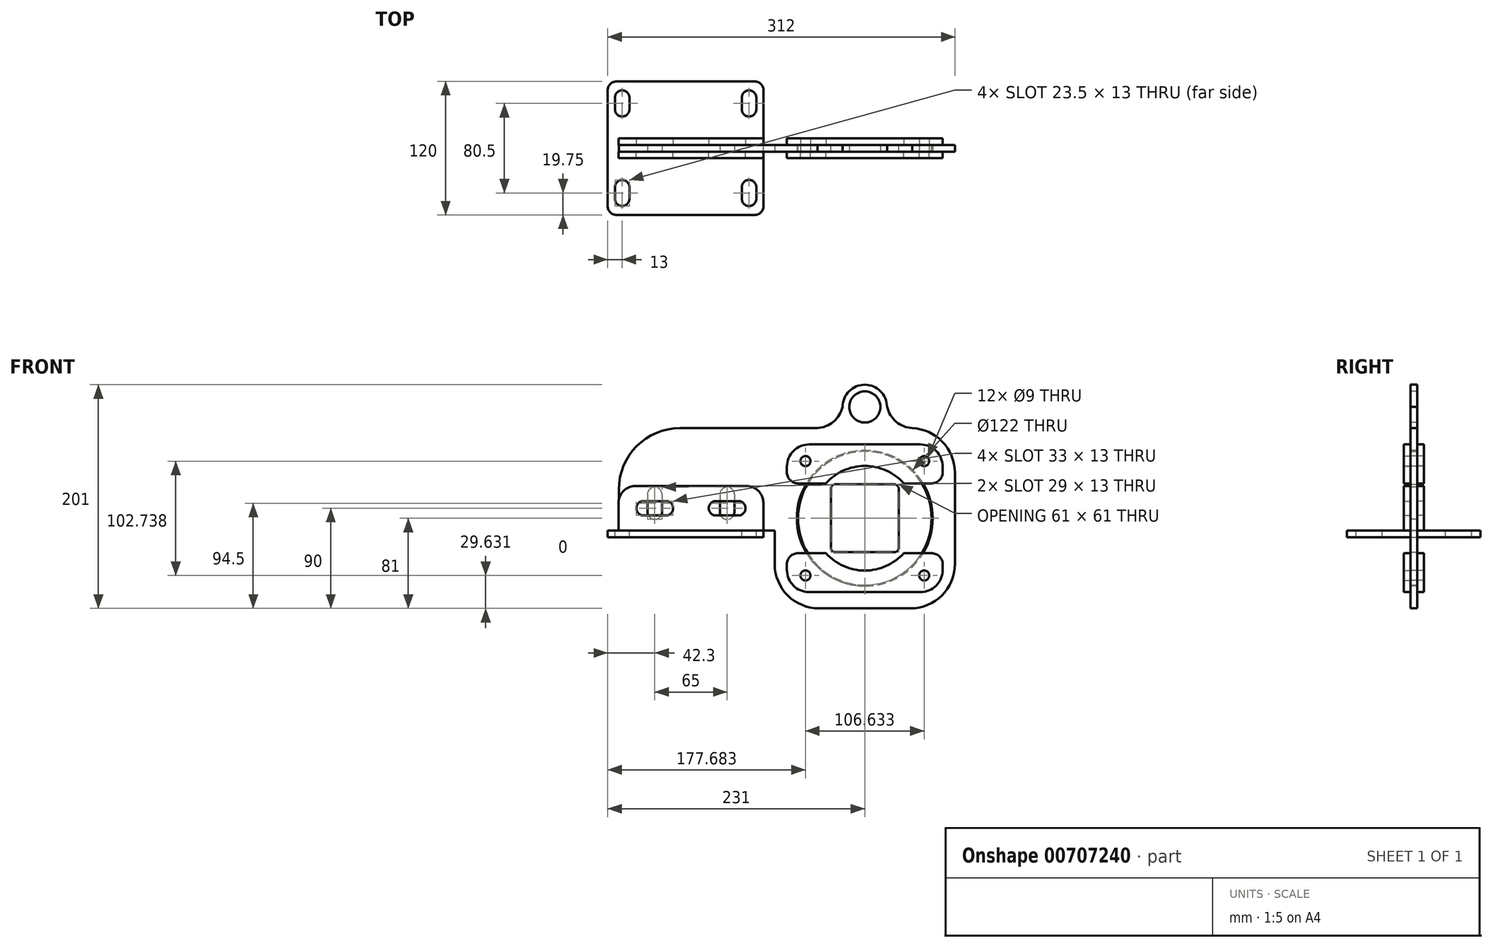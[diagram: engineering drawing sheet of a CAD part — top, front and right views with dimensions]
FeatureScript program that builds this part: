
annotation { "Feature Type Name" : "Feature", "Feature Type Description" : "" }
export const myFeature = defineFeature(function(context is Context, id is Id, definition is map)
    precondition{}
    {
        {
            var Q0;
            Q0=qCreatedBy(makeId("Front.planeOp"),FACE);
            var sketch = newSketch(context, id + "F0", { "sketchPlane" : qUnion([Q0])});
            skPoint(sketch, "E0", {"position": v(0, 0) * mm});
            skLineSegment(sketch, "E1.bottom", {"start": v(26.5, 30.5) * mm, "end": v(-26.5, 30.5) * mm});
            skLineSegment(sketch, "E1.top", {"start": v(26.5, -30.5) * mm, "end": v(-26.5, -30.5) * mm});
            skLineSegment(sketch, "E1.left", {"start": v(30.5, 26.5) * mm, "end": v(30.5, -26.5) * mm});
            skLineSegment(sketch, "E1.right", {"start": v(-30.5, 26.5) * mm, "end": v(-30.5, -26.5) * mm});
            skCircle(sketch, "E2", {"center": v(0, 0) * mm, "radius": 60 * mm});
            skPoint(sketch, "E3.visualSharp", {"position": v(-30.5, 30.5) * mm});
            skArc(sketch, "E3.filletArc", {"start": v(-26.5, 30.5) * mm, "mid": v(-29.33, 29.33) * mm, "end": v(-30.5, 26.5) * mm});
            skPoint(sketch, "E4.visualSharp", {"position": v(30.5, 30.5) * mm});
            skArc(sketch, "E4.filletArc", {"start": v(30.5, 26.5) * mm, "mid": v(29.33, 29.33) * mm, "end": v(26.5, 30.5) * mm});
            skPoint(sketch, "E5.visualSharp", {"position": v(30.5, -30.5) * mm});
            skArc(sketch, "E5.filletArc", {"start": v(26.5, -30.5) * mm, "mid": v(29.33, -29.33) * mm, "end": v(30.5, -26.5) * mm});
            skPoint(sketch, "E6.visualSharp", {"position": v(-30.5, -30.5) * mm});
            skArc(sketch, "E6.filletArc", {"start": v(-30.5, -26.5) * mm, "mid": v(-29.33, -29.33) * mm, "end": v(-26.5, -30.5) * mm});
            skSolve(sketch);
        }
        {
            var Q0;
            Q0 = qSketchRegion(id + "F0", true);
            extrude(context, id + "F1", {"entities" : qUnion([Q0]), "depth" : 6 * mm, "offsetDistance" : 25 * mm});
        }
        {
            var Q0;
            Q0=makeQuery(id+"F1.opExtrude","CAP_FACE",FACE,{"disambiguationData":[OSD([sQuery(id+"F0.wireOp",EDGE,"E1.bottom"),sQuery(id+"F0.wireOp",EDGE,"E1.top"),sQuery(id+"F0.wireOp",EDGE,"E1.left"),sQuery(id+"F0.wireOp",EDGE,"E1.right"),sQuery(id+"F0.wireOp",EDGE,"E2"),sQuery(id+"F0.wireOp",EDGE,"E3.filletArc"),sQuery(id+"F0.wireOp",EDGE,"E4.filletArc"),sQuery(id+"F0.wireOp",EDGE,"E5.filletArc"),sQuery(id+"F0.wireOp",EDGE,"E6.filletArc")])],"isStart":false});
            var sketch = newSketch(context, id + "F2", { "sketchPlane" : qUnion([Q0])});
            skCircle(sketch, "E7.0", {"center": v(0, 0) * mm, "radius": 61 * mm});
            skLineSegment(sketch, "E8.top", {"start": v(41, -81) * mm, "end": v(-41, -81) * mm});
            skLineSegment(sketch, "E8.left", {"start": v(81, 41) * mm, "end": v(81, -41) * mm});
            skLineSegment(sketch, "E8.right", {"start": v(-81, -19) * mm, "end": v(-81, -41) * mm});
            skLineSegment(sketch, "E9.bottom", {"start": v(-81, 81) * mm, "end": v(-166, 81) * mm});
            skPoint(sketch, "E10.visualSharp", {"position": v(-81, -81) * mm});
            skArc(sketch, "E10.filletArc", {"start": v(-81, -41) * mm, "mid": v(-69.28, -69.28) * mm, "end": v(-41, -81) * mm});
            skPoint(sketch, "E11.visualSharp", {"position": v(81, -81) * mm});
            skArc(sketch, "E11.filletArc", {"start": v(41, -81) * mm, "mid": v(69.28, -69.28) * mm, "end": v(81, -41) * mm});
            skPoint(sketch, "E12.visualSharp", {"position": v(81, 81) * mm});
            skArc(sketch, "E12.filletArc", {"start": v(81, 41) * mm, "mid": v(69.75, 68.81) * mm, "end": v(42.32, 80.98) * mm});
            skLineSegment(sketch, "E13", {"start": v(0, 0) * mm, "end": v(0, 100) * mm, "construction": true});
            skPoint(sketch, "E13.endSnap0", {"position": v(0, 30.5) * mm});
            skPoint(sketch, "E14.endSnap0", {"position": v(-20, 81) * mm});
            skArc(sketch, "E15.MirrorCS", {"start": v(42.5, 81) * mm, "mid": v(42.41, 80.99) * mm, "end": v(42.32, 80.98) * mm});
            skArc(sketch, "E16.trimOffspring", {"start": v(20, 100) * mm, "mid": v(0, 120) * mm, "end": v(-20, 100) * mm});
            skLineSegment(sketch, "E17.trimOffspring", {"start": v(-42.5, 81) * mm, "end": v(-81, 81) * mm});
            skCircle(sketch, "E18", {"center": v(0, 100) * mm, "radius": 14 * mm});
            skLineSegment(sketch, "E19", {"start": v(-90.5, -11) * mm, "end": v(-90.5, 81) * mm, "construction": true});
            skLineSegment(sketch, "E20", {"start": v(-211, 81) * mm, "end": v(-221, 81) * mm});
            skLineSegment(sketch, "E21", {"start": v(-221, 26) * mm, "end": v(-221, -11) * mm});
            skLineSegment(sketch, "E22", {"start": v(-221, -11) * mm, "end": v(-81, -11) * mm});
            skLineSegment(sketch, "E23", {"start": v(-81, -11) * mm, "end": v(-81, -19) * mm});
            skPoint(sketch, "E24.end.orphan", {"position": v(-211, -19) * mm});
            skPoint(sketch, "E25.orphan", {"position": v(-221, -19) * mm});
            skPoint(sketch, "E26.newPointA", {"position": v(-221, 81) * mm});
            skPoint(sketch, "E26.newPointB", {"position": v(-211, 81) * mm});
            skArc(sketch, "E26.filletArc", {"start": v(-166, 81) * mm, "mid": v(-204.9, 64.9) * mm, "end": v(-221, 26) * mm});
            skPoint(sketch, "E8.bottom.end.orphan", {"position": v(42.5, 81) * mm});
            skPoint(sketch, "E8.bottom.start.orphan", {"position": v(41, 81) * mm});
            skArc(sketch, "E27", {"start": v(-42.5, 81) * mm, "mid": v(-28.16, 86.84) * mm, "end": v(-20, 100) * mm});
            skArc(sketch, "E28.MirrorCS", {"start": v(42.5, 81) * mm, "mid": v(28.16, 86.84) * mm, "end": v(20, 100) * mm});
            skSolve(sketch);
        }
        {
            var Q0;
            Q0 = qSketchRegion(id + "F2", true);
            extrude(context, id + "F3", {"entities" : qUnion([Q0]), "oppositeDirection" : true, "depth" : 6 * mm, "offsetDistance" : 25 * mm});
        }
        {
            var Q0;
            Q0=makeQuery(id+"F3.opExtrude","CAP_FACE",FACE,{"disambiguationData":[OSD([sQuery(id+"F2.wireOp",EDGE,"E7.0"),sQuery(id+"F2.wireOp",EDGE,"E8.bottom"),sQuery(id+"F2.wireOp",EDGE,"E8.top"),sQuery(id+"F2.wireOp",EDGE,"E8.left"),sQuery(id+"F2.wireOp",EDGE,"E8.right"),sQuery(id+"F2.wireOp",EDGE,"E9.bottom"),sQuery(id+"F2.wireOp",EDGE,"E9.top"),sQuery(id+"F2.wireOp",EDGE,"E9.right"),sQuery(id+"F2.wireOp",EDGE,"338df59d-56eb-4721-a302-496fc696f20b.0.startCap"),sQuery(id+"F2.wireOp",EDGE,"338df59d-56eb-4721-a302-496fc696f20b.0.endCap"),sQuery(id+"F2.wireOp",EDGE,"338df59d-56eb-4721-a302-496fc696f20b.0.left"),sQuery(id+"F2.wireOp",EDGE,"338df59d-56eb-4721-a302-496fc696f20b.0.right"),sQuery(id+"F2.wireOp",EDGE,"338df59d-56eb-4721-a302-496fc696f20b.1.startCap"),sQuery(id+"F2.wireOp",EDGE,"338df59d-56eb-4721-a302-496fc696f20b.1.endCap"),sQuery(id+"F2.wireOp",EDGE,"338df59d-56eb-4721-a302-496fc696f20b.1.left"),sQuery(id+"F2.wireOp",EDGE,"338df59d-56eb-4721-a302-496fc696f20b.1.right"),sQuery(id+"F2.wireOp",EDGE,"E10.filletArc"),sQuery(id+"F2.wireOp",EDGE,"E11.filletArc"),sQuery(id+"F2.wireOp",EDGE,"E12.filletArc")])],"isStart":true});
            var sketch = newSketch(context, id + "F4", { "sketchPlane" : qUnion([Q0])});
            skArc(sketch, "E29.0", {"start": v(-35, -31.37) * mm, "mid": v(0, -47) * mm, "end": v(35, -31.37) * mm});
            skLineSegment(sketch, "E30", {"start": v(-60, 31.37) * mm, "end": v(-35, 31.37) * mm});
            skLineSegment(sketch, "E31", {"start": v(0, 0) * mm, "end": v(0, 41.73) * mm, "construction": true});
            skLineSegment(sketch, "E32", {"start": v(-70, 41.37) * mm, "end": v(-70, 46.37) * mm});
            skLineSegment(sketch, "E33", {"start": v(70, 41.37) * mm, "end": v(70, 46.37) * mm});
            skLineSegment(sketch, "E34", {"start": v(50, 66.37) * mm, "end": v(-50, 66.37) * mm});
            skPoint(sketch, "E35.visualSharp", {"position": v(70, 66.37) * mm});
            skArc(sketch, "E35.filletArc", {"start": v(70, 46.37) * mm, "mid": v(64.14, 60.51) * mm, "end": v(50, 66.37) * mm});
            skPoint(sketch, "E36.visualSharp", {"position": v(-70, 66.37) * mm});
            skArc(sketch, "E36.filletArc", {"start": v(-50, 66.37) * mm, "mid": v(-64.14, 60.51) * mm, "end": v(-70, 46.37) * mm});
            skPoint(sketch, "E37.visualSharp", {"position": v(-70, 31.37) * mm});
            skArc(sketch, "E37.filletArc", {"start": v(-70, 41.37) * mm, "mid": v(-67.07, 34.3) * mm, "end": v(-60, 31.37) * mm});
            skPoint(sketch, "E38.visualSharp", {"position": v(70, 31.37) * mm});
            skArc(sketch, "E38.filletArc", {"start": v(60, 31.37) * mm, "mid": v(67.07, 34.3) * mm, "end": v(70, 41.37) * mm});
            skLineSegment(sketch, "E39.trimOffspring", {"start": v(35, 31.37) * mm, "end": v(60, 31.37) * mm});
            skCircle(sketch, "E40", {"center": v(-53.32, 51.37) * mm, "radius": 4.5 * mm});
            skCircle(sketch, "E41.MirrorC", {"center": v(53.32, 51.37) * mm, "radius": 4.5 * mm});
            skLineSegment(sketch, "E42", {"start": v(0, 0) * mm, "end": v(-70.6, 0) * mm, "construction": true});
            skLineSegment(sketch, "E43", {"start": v(0, 0) * mm, "end": v(70.35, 0) * mm, "construction": true});
            skLineSegment(sketch, "E44.MirrorCS", {"start": v(70, -41.37) * mm, "end": v(70, -46.37) * mm});
            skLineSegment(sketch, "E45.MirrorCS", {"start": v(-70, -41.37) * mm, "end": v(-70, -46.37) * mm});
            skCircle(sketch, "E46.MirrorC", {"center": v(-53.32, -51.37) * mm, "radius": 4.5 * mm});
            skLineSegment(sketch, "E47.MirrorCS", {"start": v(35, -31.37) * mm, "end": v(60, -31.37) * mm});
            skArc(sketch, "E48.MirrorCS", {"start": v(60, -31.37) * mm, "mid": v(67.07, -34.3) * mm, "end": v(70, -41.37) * mm});
            skArc(sketch, "E49.MirrorCS", {"start": v(-70, -41.37) * mm, "mid": v(-67.07, -34.3) * mm, "end": v(-60, -31.37) * mm});
            skPoint(sketch, "E50.MirrorP", {"position": v(70, -31.37) * mm});
            skArc(sketch, "E51.MirrorCS", {"start": v(70, -46.37) * mm, "mid": v(64.14, -60.51) * mm, "end": v(50, -66.37) * mm});
            skPoint(sketch, "E52.MirrorP", {"position": v(-70, -66.37) * mm});
            skPoint(sketch, "E53.MirrorP", {"position": v(-70, -31.37) * mm});
            skLineSegment(sketch, "E54.MirrorCS", {"start": v(-60, -31.37) * mm, "end": v(-35, -31.37) * mm});
            skCircle(sketch, "E55.MirrorC", {"center": v(53.32, -51.37) * mm, "radius": 4.5 * mm});
            skArc(sketch, "E56.MirrorCS", {"start": v(-50, -66.37) * mm, "mid": v(-64.14, -60.51) * mm, "end": v(-70, -46.37) * mm});
            skPoint(sketch, "E57.MirrorP", {"position": v(70, -66.37) * mm});
            skLineSegment(sketch, "E58.MirrorCS", {"start": v(50, -66.37) * mm, "end": v(-50, -66.37) * mm});
            skArc(sketch, "E59.trimOffspring", {"start": v(35, 31.37) * mm, "mid": v(0, 47) * mm, "end": v(-35, 31.37) * mm});
            skSolve(sketch);
        }
        {
            var Q0;
            Q0 = qSketchRegion(id + "F4", true);
            extrude(context, id + "F5", {"entities" : qUnion([Q0]), "depth" : 6 * mm, "offsetDistance" : 25 * mm});
        }
        {
            var Q0;
            Q0=makeQuery(id+"F2.imprint","IMPRINT",FACE,{"disambiguationData":[TD([[makeQuery(id+"F2.imprint","IMPRINT",EDGE,{"derivedFrom":sQuery(id+"F2.wireOp",EDGE,"E7.0")}),-1.0]])]});
            var sketch = newSketch(context, id + "F6", { "sketchPlane" : qUnion([Q0])});
            skCircle(sketch, "E60.0", {"center": v(-53.32, 51.37) * mm, "radius": 4.5 * mm});
            skCircle(sketch, "E61.0", {"center": v(53.32, 51.37) * mm, "radius": 4.5 * mm});
            skCircle(sketch, "E62.0", {"center": v(-53.32, -51.37) * mm, "radius": 4.5 * mm});
            skCircle(sketch, "E63.0", {"center": v(53.32, -51.37) * mm, "radius": 4.5 * mm});
            skSolve(sketch);
        }
        {
            var Q0;
            Q0 = qSketchRegion(id + "F6", true);
            extrude(context, id + "F7", {"entities" : qUnion([Q0]), "operationType" : NewBodyOperationType.REMOVE, "oppositeDirection" : true, "depth" : 25 * mm, "offsetDistance" : 25 * mm});
        }
        {
            var Q0;
            Q0=makeQuery(id+"F3.opExtrude","CAP_FACE",FACE,{"disambiguationData":[OSD([sQuery(id+"F2.wireOp",EDGE,"E7.0"),sQuery(id+"F2.wireOp",EDGE,"E8.bottom"),sQuery(id+"F2.wireOp",EDGE,"E8.top"),sQuery(id+"F2.wireOp",EDGE,"E8.left"),sQuery(id+"F2.wireOp",EDGE,"E8.right"),sQuery(id+"F2.wireOp",EDGE,"E9.bottom"),sQuery(id+"F2.wireOp",EDGE,"E9.top"),sQuery(id+"F2.wireOp",EDGE,"E9.right"),sQuery(id+"F2.wireOp",EDGE,"338df59d-56eb-4721-a302-496fc696f20b.0.startCap"),sQuery(id+"F2.wireOp",EDGE,"338df59d-56eb-4721-a302-496fc696f20b.0.endCap"),sQuery(id+"F2.wireOp",EDGE,"338df59d-56eb-4721-a302-496fc696f20b.0.left"),sQuery(id+"F2.wireOp",EDGE,"338df59d-56eb-4721-a302-496fc696f20b.0.right"),sQuery(id+"F2.wireOp",EDGE,"338df59d-56eb-4721-a302-496fc696f20b.1.startCap"),sQuery(id+"F2.wireOp",EDGE,"338df59d-56eb-4721-a302-496fc696f20b.1.endCap"),sQuery(id+"F2.wireOp",EDGE,"338df59d-56eb-4721-a302-496fc696f20b.1.left"),sQuery(id+"F2.wireOp",EDGE,"338df59d-56eb-4721-a302-496fc696f20b.1.right"),sQuery(id+"F2.wireOp",EDGE,"E10.filletArc"),sQuery(id+"F2.wireOp",EDGE,"E11.filletArc"),sQuery(id+"F2.wireOp",EDGE,"E12.filletArc")])],"isStart":false});
            var sketch = newSketch(context, id + "F8", { "sketchPlane" : qUnion([Q0])});
            skLineSegment(sketch, "E64.0", {"start": v(-35, 31.37) * mm, "end": v(-60, 31.37) * mm});
            skArc(sketch, "E65.0", {"start": v(-35, 31.37) * mm, "mid": v(0, 47) * mm, "end": v(35, 31.37) * mm});
            skLineSegment(sketch, "E66.0", {"start": v(60, 31.37) * mm, "end": v(35, 31.37) * mm});
            skArc(sketch, "E67.0", {"start": v(70, 41.37) * mm, "mid": v(67.07, 34.3) * mm, "end": v(60, 31.37) * mm});
            skArc(sketch, "E68.0", {"start": v(50, 66.37) * mm, "mid": v(64.14, 60.51) * mm, "end": v(70, 46.37) * mm});
            skLineSegment(sketch, "E69.0", {"start": v(70, 41.37) * mm, "end": v(70, 46.37) * mm});
            skCircle(sketch, "E70.0", {"center": v(53.32, 51.37) * mm, "radius": 4.5 * mm});
            skLineSegment(sketch, "E71.0", {"start": v(-50, 66.37) * mm, "end": v(50, 66.37) * mm});
            skArc(sketch, "E72.0", {"start": v(-70, 46.37) * mm, "mid": v(-64.14, 60.51) * mm, "end": v(-50, 66.37) * mm});
            skLineSegment(sketch, "E73.0", {"start": v(-70, 41.37) * mm, "end": v(-70, 46.37) * mm});
            skArc(sketch, "E74.0", {"start": v(-60, 31.37) * mm, "mid": v(-67.07, 34.3) * mm, "end": v(-70, 41.37) * mm});
            skCircle(sketch, "E75.0", {"center": v(-53.32, 51.37) * mm, "radius": 4.5 * mm});
            skLineSegment(sketch, "E76.0", {"start": v(-35, -31.37) * mm, "end": v(-60, -31.37) * mm});
            skArc(sketch, "E77.0", {"start": v(35, -31.37) * mm, "mid": v(0, -47) * mm, "end": v(-35, -31.37) * mm});
            skLineSegment(sketch, "E78.0", {"start": v(60, -31.37) * mm, "end": v(35, -31.37) * mm});
            skArc(sketch, "E79.0", {"start": v(70, -41.37) * mm, "mid": v(67.07, -34.3) * mm, "end": v(60, -31.37) * mm});
            skLineSegment(sketch, "E80.0", {"start": v(70, -41.37) * mm, "end": v(70, -46.37) * mm});
            skArc(sketch, "E81.0", {"start": v(50, -66.37) * mm, "mid": v(64.14, -60.51) * mm, "end": v(70, -46.37) * mm});
            skCircle(sketch, "E82.0", {"center": v(53.32, -51.37) * mm, "radius": 4.5 * mm});
            skLineSegment(sketch, "E83.0", {"start": v(-50, -66.37) * mm, "end": v(50, -66.37) * mm});
            skArc(sketch, "E84.0", {"start": v(-70, -46.37) * mm, "mid": v(-64.14, -60.51) * mm, "end": v(-50, -66.37) * mm});
            skCircle(sketch, "E85.0.0", {"center": v(-53.32, -51.37) * mm, "radius": 4.5 * mm});
            skLineSegment(sketch, "E86.0", {"start": v(-70, -41.37) * mm, "end": v(-70, -46.37) * mm});
            skArc(sketch, "E87.0", {"start": v(-60, -31.37) * mm, "mid": v(-67.07, -34.3) * mm, "end": v(-70, -41.37) * mm});
            skSolve(sketch);
        }
        {
            var Q0;
            Q0 = qSketchRegion(id + "F8", true);
            extrude(context, id + "F9", {"entities" : qUnion([Q0]), "depth" : 6 * mm, "offsetDistance" : 25 * mm});
        }
        {
            var Q0;
            Q0=makeQuery(id+"F3.opExtrude","CAP_FACE",FACE,{"disambiguationData":[OSD([sQuery(id+"F2.wireOp",EDGE,"E7.0"),sQuery(id+"F2.wireOp",EDGE,"E8.bottom"),sQuery(id+"F2.wireOp",EDGE,"E8.top"),sQuery(id+"F2.wireOp",EDGE,"E8.left"),sQuery(id+"F2.wireOp",EDGE,"E8.right"),sQuery(id+"F2.wireOp",EDGE,"E9.bottom"),sQuery(id+"F2.wireOp",EDGE,"E9.top"),sQuery(id+"F2.wireOp",EDGE,"E9.right"),sQuery(id+"F2.wireOp",EDGE,"338df59d-56eb-4721-a302-496fc696f20b.0.startCap"),sQuery(id+"F2.wireOp",EDGE,"338df59d-56eb-4721-a302-496fc696f20b.0.endCap"),sQuery(id+"F2.wireOp",EDGE,"338df59d-56eb-4721-a302-496fc696f20b.0.left"),sQuery(id+"F2.wireOp",EDGE,"338df59d-56eb-4721-a302-496fc696f20b.0.right"),sQuery(id+"F2.wireOp",EDGE,"338df59d-56eb-4721-a302-496fc696f20b.1.startCap"),sQuery(id+"F2.wireOp",EDGE,"338df59d-56eb-4721-a302-496fc696f20b.1.endCap"),sQuery(id+"F2.wireOp",EDGE,"338df59d-56eb-4721-a302-496fc696f20b.1.left"),sQuery(id+"F2.wireOp",EDGE,"338df59d-56eb-4721-a302-496fc696f20b.1.right"),sQuery(id+"F2.wireOp",EDGE,"E10.filletArc"),sQuery(id+"F2.wireOp",EDGE,"E11.filletArc"),sQuery(id+"F2.wireOp",EDGE,"E12.filletArc")])],"isStart":true});
            var sketch = newSketch(context, id + "F10", { "sketchPlane" : qUnion([Q0])});
            skLineSegment(sketch, "E88.0", {"start": v(-91.2, -11) * mm, "end": v(-221.2, -11) * mm});
            skArc(sketch, "E89.0", {"start": v(-178.7, 15.5) * mm, "mid": v(-172.2, 9) * mm, "end": v(-178.7, 2.5) * mm});
            skLineSegment(sketch, "E90.0", {"start": v(-198.7, 2.5) * mm, "end": v(-178.7, 2.5) * mm});
            skArc(sketch, "E91.0", {"start": v(-198.7, 2.5) * mm, "mid": v(-205.2, 9) * mm, "end": v(-198.7, 15.5) * mm});
            skLineSegment(sketch, "E92.0", {"start": v(-198.7, 15.5) * mm, "end": v(-178.7, 15.5) * mm});
            skLineSegment(sketch, "E93.0", {"start": v(-133.7, 15.5) * mm, "end": v(-113.7, 15.5) * mm});
            skArc(sketch, "E94.0", {"start": v(-133.7, 2.5) * mm, "mid": v(-140.2, 9) * mm, "end": v(-133.7, 15.5) * mm});
            skLineSegment(sketch, "E95.0", {"start": v(-133.7, 2.5) * mm, "end": v(-113.7, 2.5) * mm});
            skArc(sketch, "E96.0", {"start": v(-113.7, 15.5) * mm, "mid": v(-107.2, 9) * mm, "end": v(-113.7, 2.5) * mm});
            skLineSegment(sketch, "E97", {"start": v(-221.2, -11) * mm, "end": v(-221.2, 14) * mm});
            skLineSegment(sketch, "E98", {"start": v(-91.2, -11) * mm, "end": v(-91.2, 14) * mm});
            skLineSegment(sketch, "E99", {"start": v(-106.2, 29) * mm, "end": v(-206.2, 29) * mm});
            skPoint(sketch, "E100.visualSharp", {"position": v(-221.2, 29) * mm});
            skArc(sketch, "E100.filletArc", {"start": v(-206.2, 29) * mm, "mid": v(-216.8, 24.6) * mm, "end": v(-221.2, 14) * mm});
            skPoint(sketch, "E101.visualSharp", {"position": v(-91.2, 29) * mm});
            skArc(sketch, "E101.filletArc", {"start": v(-91.2, 14) * mm, "mid": v(-95.6, 24.6) * mm, "end": v(-106.2, 29) * mm});
            skSolve(sketch);
        }
        {
            var Q0;
            Q0 = qSketchRegion(id + "F10", true);
            extrude(context, id + "F11", {"entities" : qUnion([Q0]), "depth" : 6 * mm, "offsetDistance" : 25 * mm});
        }
        {
            var Q0;
            {var subQ2=sQuery(id+"F10.wireOp",EDGE,"E98");Q0=makeQuery(id+"F10.imprint","IMPRINT",FACE,{"disambiguationData":[TD([[makeQuery(id+"F10.imprint","IMPRINT",EDGE,{"derivedFrom":subQ2}),-1.0]])]});}
            var sketch = newSketch(context, id + "F12", { "sketchPlane" : qUnion([Q0])});
            skLineSegment(sketch, "E102", {"start": v(-188.7, 21.5) * mm, "end": v(-188.7, 5.5) * mm, "construction": true});
            skLineSegment(sketch, "E103", {"start": v(-123.7, 21.5) * mm, "end": v(-123.7, 5.5) * mm, "construction": true});
            skArc(sketch, "E104.0.startCap", {"start": v(-195.2, 21.5) * mm, "mid": v(-188.7, 28) * mm, "end": v(-182.2, 21.5) * mm});
            skArc(sketch, "E104.0.endCap", {"start": v(-182.2, 5.5) * mm, "mid": v(-188.7, -1) * mm, "end": v(-195.2, 5.5) * mm});
            skLineSegment(sketch, "E104.0.left", {"start": v(-182.2, 21.5) * mm, "end": v(-182.2, 5.5) * mm});
            skLineSegment(sketch, "E104.0.right", {"start": v(-195.2, 21.5) * mm, "end": v(-195.2, 5.5) * mm});
            skArc(sketch, "E104.1.startCap", {"start": v(-130.2, 21.5) * mm, "mid": v(-123.7, 28) * mm, "end": v(-117.2, 21.5) * mm});
            skArc(sketch, "E104.1.endCap", {"start": v(-117.2, 5.5) * mm, "mid": v(-123.7, -1) * mm, "end": v(-130.2, 5.5) * mm});
            skLineSegment(sketch, "E104.1.left", {"start": v(-117.2, 21.5) * mm, "end": v(-117.2, 5.5) * mm});
            skLineSegment(sketch, "E104.1.right", {"start": v(-130.2, 21.5) * mm, "end": v(-130.2, 5.5) * mm});
            skSolve(sketch);
        }
        {
            var Q0;
            Q0 = qSketchRegion(id + "F12", true);
            extrude(context, id + "F13", {"entities" : qUnion([Q0]), "operationType" : NewBodyOperationType.REMOVE, "oppositeDirection" : true, "depth" : 25 * mm, "offsetDistance" : 25 * mm});
        }
        {
            var Q0;
            Q0=makeQuery(id+"F3.opExtrude","CAP_FACE",FACE,{"disambiguationData":[OSD([sQuery(id+"F2.wireOp",EDGE,"E7.0"),sQuery(id+"F2.wireOp",EDGE,"E8.bottom"),sQuery(id+"F2.wireOp",EDGE,"E8.top"),sQuery(id+"F2.wireOp",EDGE,"E8.left"),sQuery(id+"F2.wireOp",EDGE,"E8.right"),sQuery(id+"F2.wireOp",EDGE,"E9.bottom"),sQuery(id+"F2.wireOp",EDGE,"E10.filletArc"),sQuery(id+"F2.wireOp",EDGE,"E11.filletArc"),sQuery(id+"F2.wireOp",EDGE,"E12.filletArc"),sQuery(id+"F2.wireOp",EDGE,"E14"),sQuery(id+"F2.wireOp",EDGE,"E15.MirrorCS"),sQuery(id+"F2.wireOp",EDGE,"E16.trimOffspring"),sQuery(id+"F2.wireOp",EDGE,"E17.trimOffspring"),sQuery(id+"F2.wireOp",EDGE,"E18"),sQuery(id+"F2.wireOp",EDGE,"E20"),sQuery(id+"F2.wireOp",EDGE,"E21"),sQuery(id+"F2.wireOp",EDGE,"E22"),sQuery(id+"F2.wireOp",EDGE,"E23")])],"isStart":false});
            var sketch = newSketch(context, id + "F14", { "sketchPlane" : qUnion([Q0])});
            skArc(sketch, "E105.0", {"start": v(91.2, 14) * mm, "mid": v(95.6, 24.6) * mm, "end": v(106.2, 29) * mm});
            skLineSegment(sketch, "E106.0", {"start": v(106.2, 29) * mm, "end": v(206.2, 29) * mm});
            skArc(sketch, "E107.0", {"start": v(206.2, 29) * mm, "mid": v(216.8, 24.6) * mm, "end": v(221.2, 14) * mm});
            skLineSegment(sketch, "E108.0", {"start": v(221.2, -11) * mm, "end": v(221.2, 14) * mm});
            skLineSegment(sketch, "E109.0", {"start": v(91.2, -11) * mm, "end": v(221.2, -11) * mm});
            skLineSegment(sketch, "E110.0", {"start": v(91.2, -11) * mm, "end": v(91.2, 14) * mm});
            skArc(sketch, "E111.0", {"start": v(113.7, 15.5) * mm, "mid": v(107.2, 9) * mm, "end": v(113.7, 2.5) * mm});
            skArc(sketch, "E112.0", {"start": v(133.7, 2.5) * mm, "mid": v(140.2, 9) * mm, "end": v(133.7, 15.5) * mm});
            skLineSegment(sketch, "E113.0", {"start": v(133.7, 15.5) * mm, "end": v(113.7, 15.5) * mm});
            skLineSegment(sketch, "E114.0", {"start": v(133.7, 2.5) * mm, "end": v(113.7, 2.5) * mm});
            skArc(sketch, "E115.0", {"start": v(178.7, 15.5) * mm, "mid": v(172.2, 9) * mm, "end": v(178.7, 2.5) * mm});
            skArc(sketch, "E116.0", {"start": v(198.7, 2.5) * mm, "mid": v(205.2, 9) * mm, "end": v(198.7, 15.5) * mm});
            skLineSegment(sketch, "E117.0", {"start": v(198.7, 15.5) * mm, "end": v(178.7, 15.5) * mm});
            skLineSegment(sketch, "E118.0", {"start": v(198.7, 2.5) * mm, "end": v(178.7, 2.5) * mm});
            skSolve(sketch);
        }
        {
            var Q0;
            Q0 = qSketchRegion(id + "F14", true);
            extrude(context, id + "F15", {"entities" : qUnion([Q0]), "depth" : 6 * mm, "offsetDistance" : 25 * mm});
        }
        {
            var Q0;
            Q0=makeQuery(id+"F3.opExtrude","SWEPT_FACE",FACE,{"disambiguationData":[OSD([sQuery(id+"F2.wireOp",EDGE,"E22")])]});
            var sketch = newSketch(context, id + "F16", { "sketchPlane" : qUnion([Q0])});
            skLineSegment(sketch, "E119", {"start": v(-231, 55) * mm, "end": v(-231, -49) * mm});
            skLineSegment(sketch, "E120", {"start": v(-223, 63) * mm, "end": v(-99, 63) * mm});
            skLineSegment(sketch, "E121", {"start": v(-91, 55) * mm, "end": v(-91, -49) * mm});
            skLineSegment(sketch, "E122", {"start": v(-99, -57) * mm, "end": v(-223, -57) * mm});
            skLineSegment(sketch, "E123.0", {"start": v(-104, 48.5) * mm, "end": v(-104, 38) * mm});
            skLineSegment(sketch, "E124.0", {"start": v(-218, 48.5) * mm, "end": v(-218, 38) * mm});
            skLineSegment(sketch, "E125", {"start": v(-218.13, 38) * mm, "end": v(-218, 38) * mm, "construction": true});
            skLineSegment(sketch, "E126.trimOffspring", {"start": v(-218, -32) * mm, "end": v(-218, -42.5) * mm});
            skLineSegment(sketch, "E127.trimOffspring", {"start": v(-104, -32) * mm, "end": v(-104, -42.5) * mm});
            skLineSegment(sketch, "E128.trimOffspring", {"start": v(-104.16, 38) * mm, "end": v(-104, 38) * mm, "construction": true});
            skArc(sketch, "E129.0.startCap", {"start": v(-224.5, 48.5) * mm, "mid": v(-218, 55) * mm, "end": v(-211.5, 48.5) * mm});
            skArc(sketch, "E129.0.endCap", {"start": v(-211.5, 38) * mm, "mid": v(-218, 31.5) * mm, "end": v(-224.5, 38) * mm});
            skLineSegment(sketch, "E129.0.left", {"start": v(-211.5, 48.5) * mm, "end": v(-211.5, 38) * mm});
            skLineSegment(sketch, "E129.0.right", {"start": v(-224.5, 48.5) * mm, "end": v(-224.5, 38) * mm});
            skArc(sketch, "E129.1.startCap", {"start": v(-110.5, 48.5) * mm, "mid": v(-104, 55) * mm, "end": v(-97.5, 48.5) * mm});
            skArc(sketch, "E129.1.endCap", {"start": v(-97.5, 38) * mm, "mid": v(-104, 31.5) * mm, "end": v(-110.5, 38) * mm});
            skLineSegment(sketch, "E129.1.left", {"start": v(-97.5, 48.5) * mm, "end": v(-97.5, 38) * mm});
            skLineSegment(sketch, "E129.1.right", {"start": v(-110.5, 48.5) * mm, "end": v(-110.5, 38) * mm});
            skArc(sketch, "E129.2.startCap", {"start": v(-110.5, -32) * mm, "mid": v(-104, -25.5) * mm, "end": v(-97.5, -32) * mm});
            skArc(sketch, "E129.2.endCap", {"start": v(-97.5, -42.5) * mm, "mid": v(-104, -49) * mm, "end": v(-110.5, -42.5) * mm});
            skLineSegment(sketch, "E129.2.left", {"start": v(-97.5, -32) * mm, "end": v(-97.5, -42.5) * mm});
            skLineSegment(sketch, "E129.2.right", {"start": v(-110.5, -32) * mm, "end": v(-110.5, -42.5) * mm});
            skArc(sketch, "E129.3.startCap", {"start": v(-224.5, -32) * mm, "mid": v(-218, -25.5) * mm, "end": v(-211.5, -32) * mm});
            skArc(sketch, "E129.3.endCap", {"start": v(-211.5, -42.5) * mm, "mid": v(-218, -49) * mm, "end": v(-224.5, -42.5) * mm});
            skLineSegment(sketch, "E129.3.left", {"start": v(-211.5, -32) * mm, "end": v(-211.5, -42.5) * mm});
            skLineSegment(sketch, "E129.3.right", {"start": v(-224.5, -32) * mm, "end": v(-224.5, -42.5) * mm});
            skPoint(sketch, "E130.visualSharp", {"position": v(-231, -57) * mm});
            skArc(sketch, "E130.filletArc", {"start": v(-231, -49) * mm, "mid": v(-228.66, -54.66) * mm, "end": v(-223, -57) * mm});
            skPoint(sketch, "E131.visualSharp", {"position": v(-91, -57) * mm});
            skArc(sketch, "E131.filletArc", {"start": v(-99, -57) * mm, "mid": v(-93.34, -54.66) * mm, "end": v(-91, -49) * mm});
            skPoint(sketch, "E132.visualSharp", {"position": v(-91, 63) * mm});
            skArc(sketch, "E132.filletArc", {"start": v(-91, 55) * mm, "mid": v(-93.34, 60.66) * mm, "end": v(-99, 63) * mm});
            skPoint(sketch, "E133.visualSharp", {"position": v(-231, 63) * mm});
            skArc(sketch, "E133.filletArc", {"start": v(-223, 63) * mm, "mid": v(-228.66, 60.66) * mm, "end": v(-231, 55) * mm});
            skSolve(sketch);
        }
        {
            var Q0;
            Q0 = qSketchRegion(id + "F16", true);
            extrude(context, id + "F17", {"entities" : qUnion([Q0]), "depth" : 6 * mm, "offsetDistance" : 25 * mm});
        }
    });
